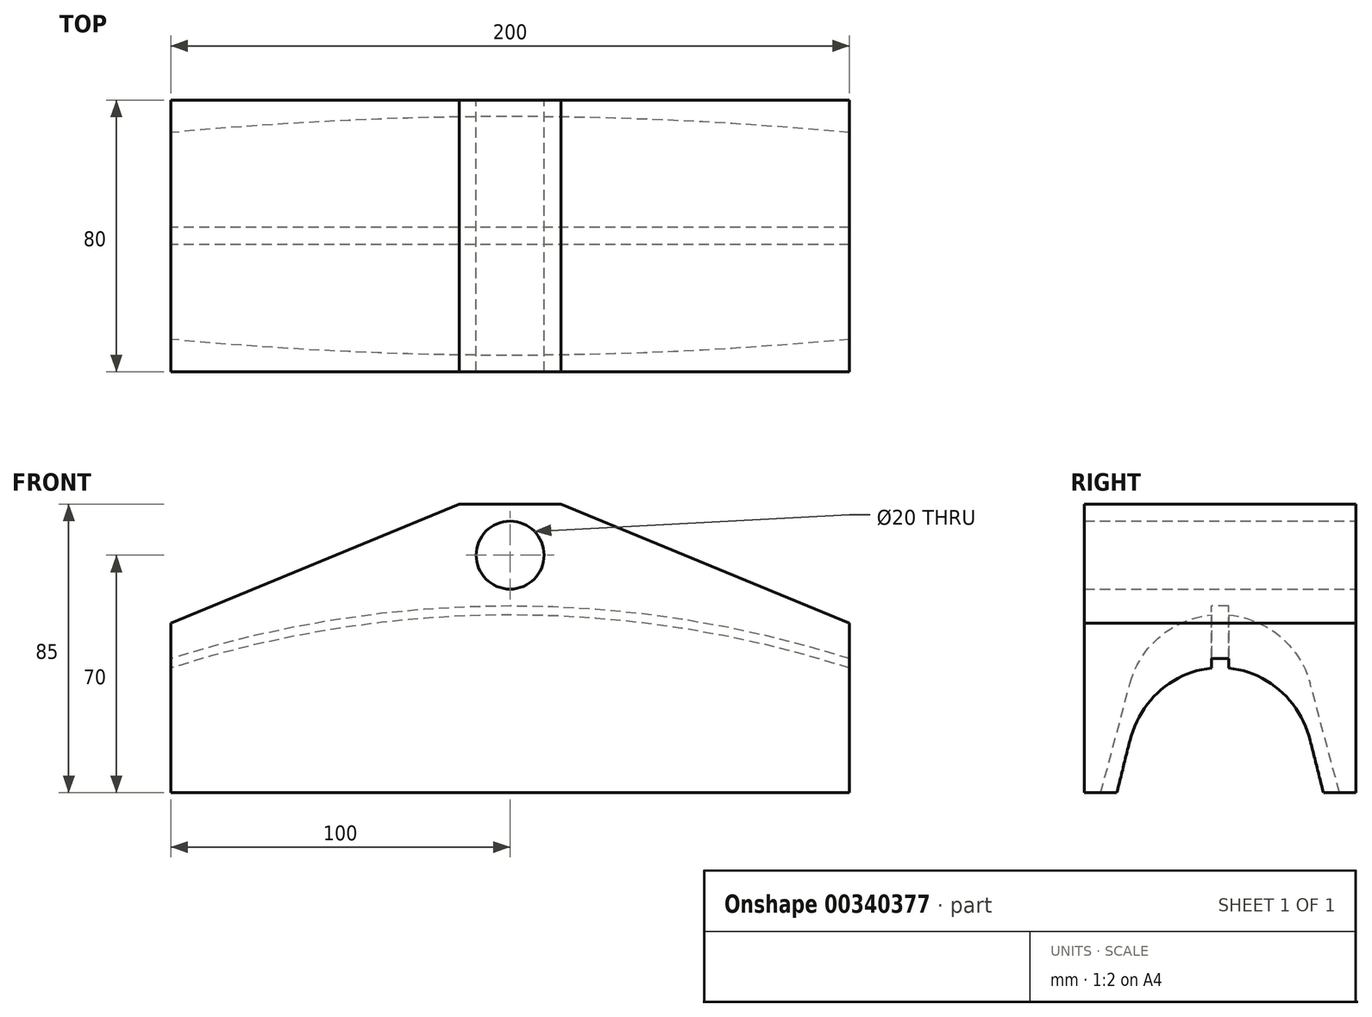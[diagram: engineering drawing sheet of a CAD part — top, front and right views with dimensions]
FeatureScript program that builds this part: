
annotation { "Feature Type Name" : "Feature", "Feature Type Description" : "" }
export const myFeature = defineFeature(function(context is Context, id is Id, definition is map)
    precondition{}
    {
        {
            var Q0;
            Q0=qCreatedBy(makeId("Front.planeOp"),FACE);
            var sketch = newSketch(context, id + "F0", { "sketchPlane" : qUnion([Q0])});
            skCircle(sketch, "E0", {"center": v(0, 0) * mm, "radius": 300 * mm, "construction": true});
            skLineSegment(sketch, "E1", {"start": v(0, 0) * mm, "end": v(0, 345) * mm, "construction": true});
            skCircle(sketch, "E2", {"center": v(0, 345) * mm, "radius": 10 * mm});
            skCircle(sketch, "E3", {"center": v(0, 0) * mm, "radius": 325 * mm, "construction": true});
            skPoint(sketch, "E4", {"position": v(0, 325) * mm});
            skPoint(sketch, "E5", {"position": v(0, 335) * mm});
            skLineSegment(sketch, "E6", {"start": v(-15, 360) * mm, "end": v(0, 360) * mm});
            skLineSegment(sketch, "E7", {"start": v(0, 345) * mm, "end": v(0, 360) * mm, "construction": true});
            skLineSegment(sketch, "E8", {"start": v(-100, 325) * mm, "end": v(-100, 275) * mm});
            skLineSegment(sketch, "E9", {"start": v(-100, 275) * mm, "end": v(0, 275) * mm});
            skLineSegment(sketch, "E10", {"start": v(-15, 360) * mm, "end": v(-100, 325) * mm});
            skLineSegment(sketch, "E11.MirrorCS", {"start": v(15, 360) * mm, "end": v(0, 360) * mm});
            skLineSegment(sketch, "E12.MirrorCS", {"start": v(15, 360) * mm, "end": v(100, 325) * mm});
            skLineSegment(sketch, "E13.MirrorCS", {"start": v(100, 325) * mm, "end": v(100, 275) * mm});
            skLineSegment(sketch, "E14.MirrorCS", {"start": v(100, 275) * mm, "end": v(0, 275) * mm});
            skSolve(sketch);
        }
        {
            var Q0;
            Q0=makeQuery(id+"F0.imprint","IMPRINT",FACE,{"disambiguationData":[TD([[makeQuery(id+"F0.imprint","IMPRINT",EDGE,{"derivedFrom":sQuery(id+"F0.wireOp",EDGE,"E2")}),-1.0]])]});
            extrude(context, id + "F1", {"entities" : qUnion([Q0]), "endBound" : BoundingType.SYMMETRIC, "depth" : 80 * mm});
        }
        {
            var Q0;
            Q0=qCreatedBy(makeId("Right.planeOp"),FACE);
            var sketch = newSketch(context, id + "F2", { "sketchPlane" : qUnion([Q0])});
            skArc(sketch, "E15", {"start": v(26.56, 307.12) * mm, "mid": v(17.72, 321.03) * mm, "end": v(2.5, 327.39) * mm});
            skLineSegment(sketch, "E16", {"start": v(0, 300) * mm, "end": v(0, 260) * mm, "construction": true});
            skLineSegment(sketch, "E17", {"start": v(39.19, 260) * mm, "end": v(-39.19, 260) * mm});
            skLineSegment(sketch, "E18", {"start": v(26.56, 307.12) * mm, "end": v(39.19, 260) * mm});
            skLineSegment(sketch, "E19", {"start": v(-26.56, 307.12) * mm, "end": v(-39.19, 260) * mm});
            skLineSegment(sketch, "E20", {"start": v(-2.5, 327.39) * mm, "end": v(-2.5, 330) * mm});
            skLineSegment(sketch, "E21", {"start": v(-2.5, 330) * mm, "end": v(2.5, 330) * mm});
            skLineSegment(sketch, "E22", {"start": v(2.5, 330) * mm, "end": v(2.5, 327.39) * mm});
            skArc(sketch, "E23.trimOffspring", {"start": v(-2.5, 327.39) * mm, "mid": v(-17.72, 321.03) * mm, "end": v(-26.56, 307.12) * mm});
            skLineSegment(sketch, "E24", {"start": v(0, 0) * mm, "end": v(-60.92, 0) * mm, "construction": true});
            skSolve(sketch);
        }
        {
            var Q0;
            Q0 = qSketchRegion(id + "F2", true);
            var Q1;
            Q1=sQuery(id+"F0.wireOp",EDGE,"E0");
            revolve(context, id + "F3", {"operationType" : NewBodyOperationType.REMOVE, "entities" : qUnion([Q0]), "axis" : qUnion([Q1]), "revolveType" : RevolveType.FULL, "oppositeDirection" : true});
        }
    });
